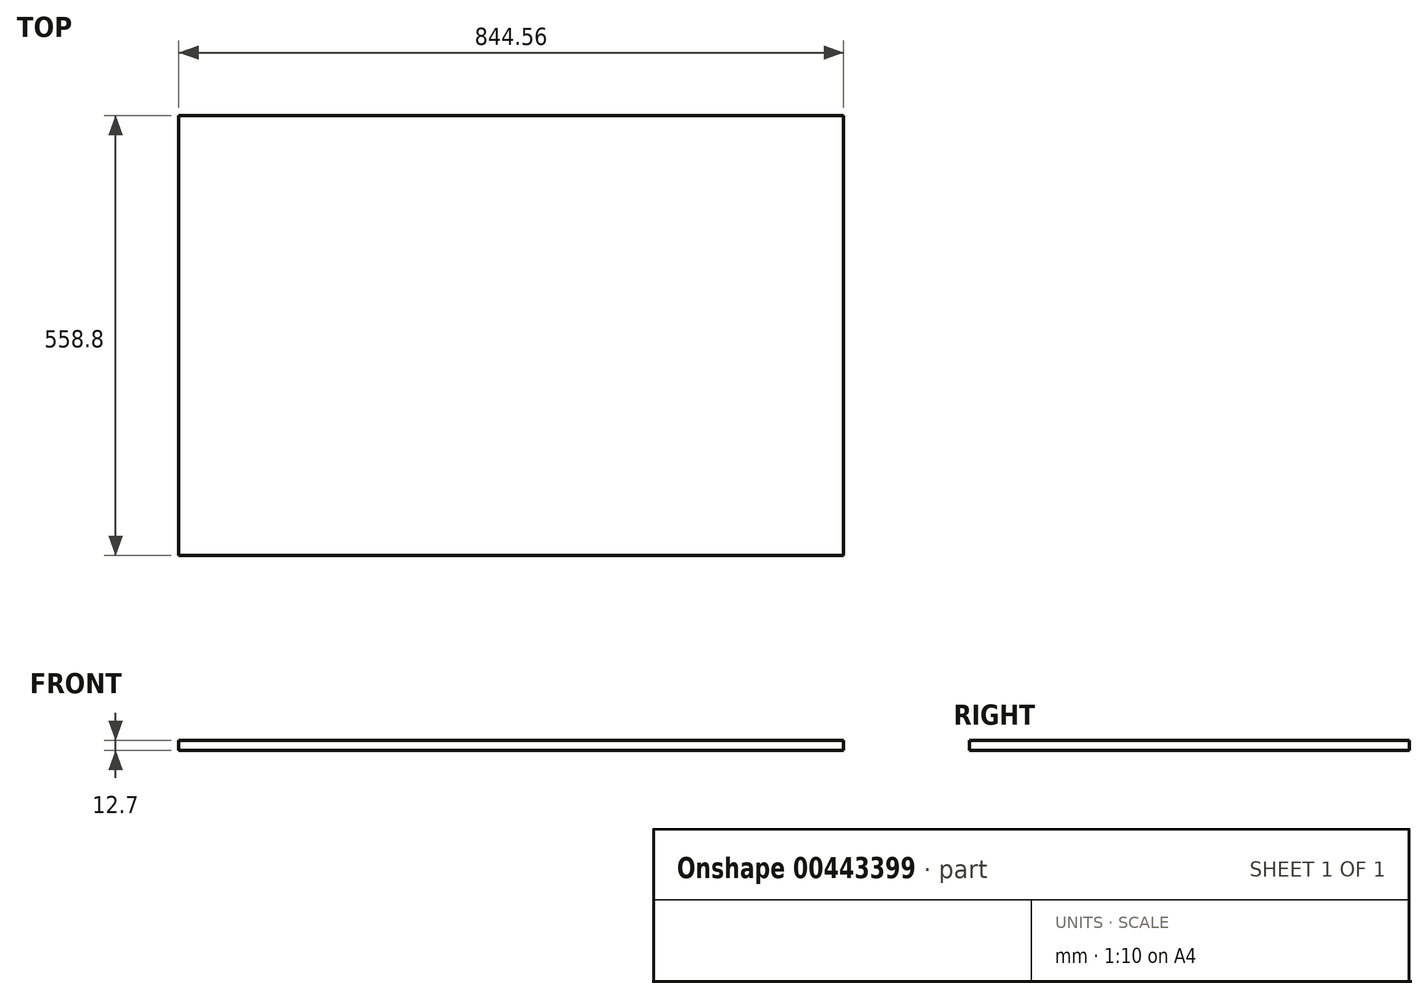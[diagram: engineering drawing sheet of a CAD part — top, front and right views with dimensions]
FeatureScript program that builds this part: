
annotation { "Feature Type Name" : "Feature", "Feature Type Description" : "" }
export const myFeature = defineFeature(function(context is Context, id is Id, definition is map)
    precondition{}
    {
        {
            var Q0;
            Q0=qCreatedBy(makeId("Top.planeOp"),FACE);
            var sketch = newSketch(context, id + "F0", { "sketchPlane" : qUnion([Q0])});
            skLineSegment(sketch, "E0.bottom", {"start": v(422.28, -279.4) * mm, "end": v(-422.28, -279.4) * mm});
            skLineSegment(sketch, "E0.top", {"start": v(422.28, 279.4) * mm, "end": v(-422.28, 279.4) * mm});
            skLineSegment(sketch, "E0.left", {"start": v(422.28, -279.4) * mm, "end": v(422.28, 279.4) * mm});
            skLineSegment(sketch, "E0.right", {"start": v(-422.28, -279.4) * mm, "end": v(-422.28, 279.4) * mm});
            skPoint(sketch, "E0.middle", {"position": v(0, 0) * mm});
            skSolve(sketch);
        }
        {
            var Q0;
            Q0 = qSketchRegion(id + "F0", true);
            extrude(context, id + "F1", {"entities" : qUnion([Q0]), "depth" : 12.7 * mm});
        }
    });
